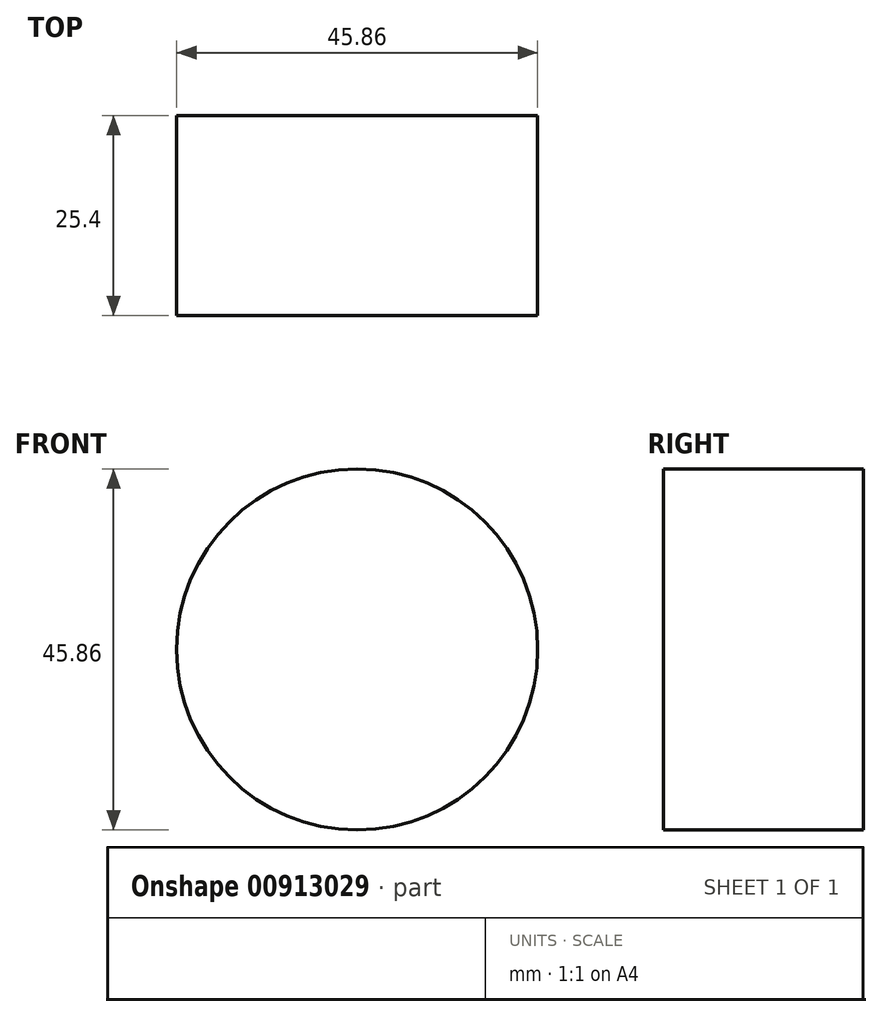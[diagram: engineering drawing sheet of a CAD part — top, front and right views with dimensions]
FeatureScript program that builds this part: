
annotation { "Feature Type Name" : "Feature", "Feature Type Description" : "" }
export const myFeature = defineFeature(function(context is Context, id is Id, definition is map)
    precondition{}
    {
        {
            var Q0;
            Q0=qCreatedBy(makeId("Front.planeOp"),FACE);
            var sketch = newSketch(context, id + "F0", { "sketchPlane" : qUnion([Q0])});
            skCircle(sketch, "E0", {"center": v(0, 0) * mm, "radius": 22.93 * mm});
            skSolve(sketch);
        }
        {
            var Q0;
            Q0=makeQuery(id+"F0.imprint","IMPRINT",FACE,{"disambiguationData":[TD([[makeQuery(id+"F0.imprint","IMPRINT",EDGE,{"derivedFrom":sQuery(id+"F0.wireOp",EDGE,"E0")}),1.0]])]});
            extrude(context, id + "F1", {"entities" : qUnion([Q0]), "depth" : 25.4 * mm, "offsetDistance" : 25.4 * mm});
        }
    });
